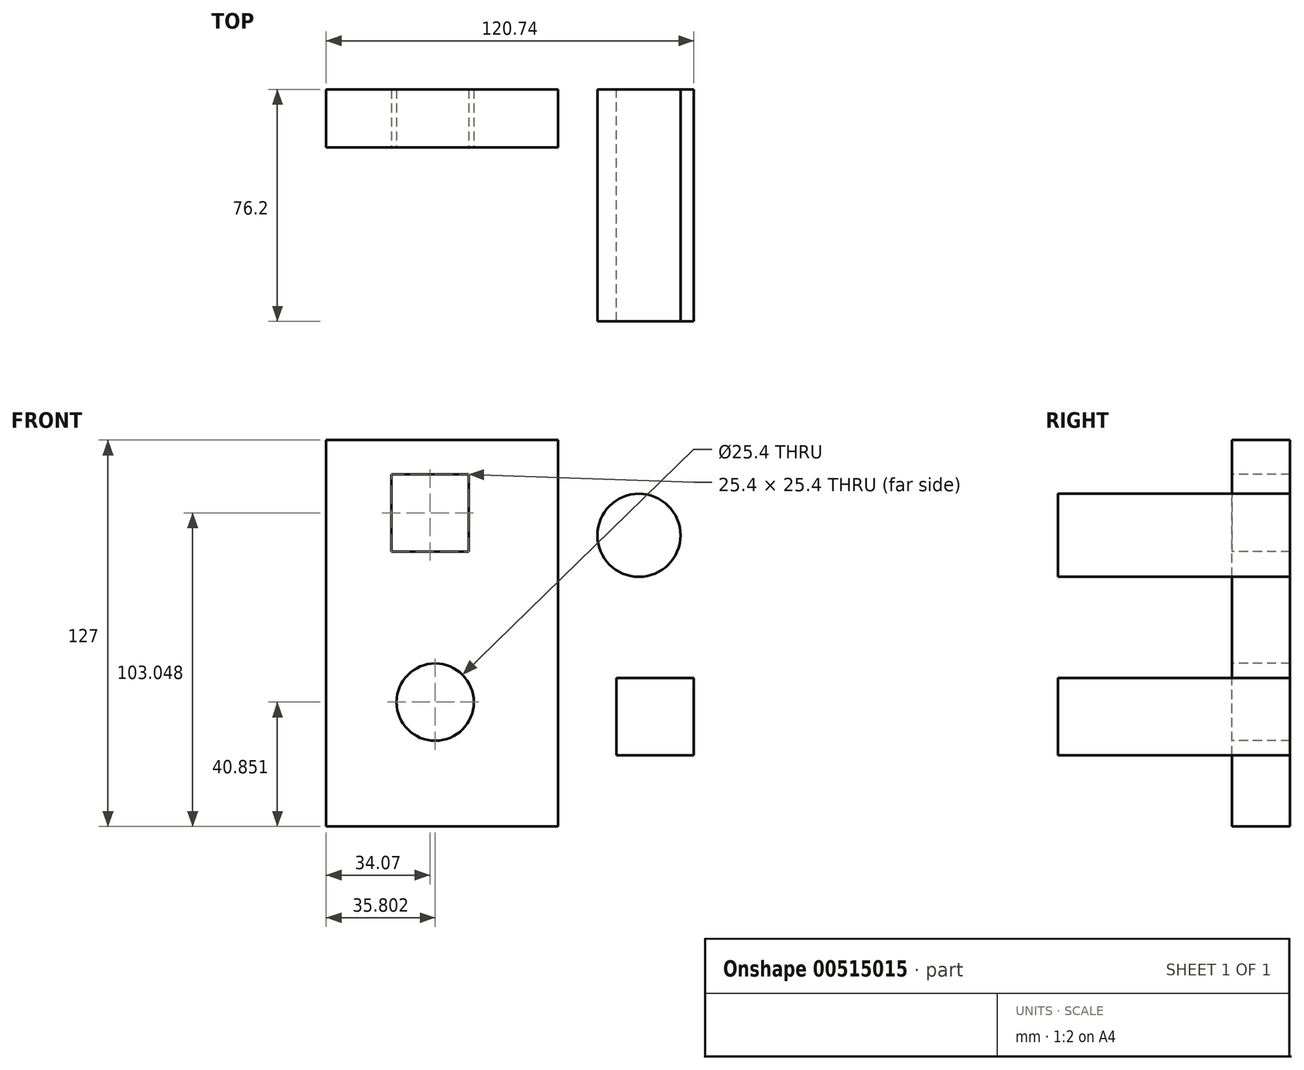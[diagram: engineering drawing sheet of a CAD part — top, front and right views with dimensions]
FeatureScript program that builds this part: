
annotation { "Feature Type Name" : "Feature", "Feature Type Description" : "" }
export const myFeature = defineFeature(function(context is Context, id is Id, definition is map)
    precondition{}
    {
        {
            var Q0;
            Q0=qCreatedBy(makeId("Front.planeOp"),FACE);
            var sketch = newSketch(context, id + "F0", { "sketchPlane" : qUnion([Q0])});
            skLineSegment(sketch, "E0", {"start": v(-71.8, 77.54) * mm, "end": v(-71.8, -49.46) * mm});
            skLineSegment(sketch, "E1", {"start": v(-71.8, -49.46) * mm, "end": v(4.4, -49.46) * mm});
            skLineSegment(sketch, "E2", {"start": v(4.4, -49.46) * mm, "end": v(4.4, 77.54) * mm});
            skLineSegment(sketch, "E3", {"start": v(4.4, 77.54) * mm, "end": v(-71.8, 77.54) * mm});
            skSolve(sketch);
        }
        {
            var Q0;
            Q0 = qSketchRegion(id + "F0", true);
            extrude(context, id + "F1", {"entities" : qUnion([Q0]), "depth" : 19.05 * mm, "offsetDistance" : 25.4 * mm});
        }
        {
            var Q0;
            Q0=makeQuery(id+"F1.opExtrude","CAP_FACE",FACE,{"disambiguationData":[OSD([sQuery(id+"F0.wireOp",EDGE,"E0"),sQuery(id+"F0.wireOp",EDGE,"E1"),sQuery(id+"F0.wireOp",EDGE,"E2"),sQuery(id+"F0.wireOp",EDGE,"E3")])],"isStart":false});
            var sketch = newSketch(context, id + "F2", { "sketchPlane" : qUnion([Q0])});
            skLineSegment(sketch, "E4.bottom", {"start": v(-50.43, 66.29) * mm, "end": v(-25.03, 66.29) * mm});
            skLineSegment(sketch, "E4.top", {"start": v(-50.43, 40.89) * mm, "end": v(-25.03, 40.89) * mm});
            skLineSegment(sketch, "E4.left", {"start": v(-50.43, 66.29) * mm, "end": v(-50.43, 40.89) * mm});
            skLineSegment(sketch, "E4.right", {"start": v(-25.03, 66.29) * mm, "end": v(-25.03, 40.89) * mm});
            skSolve(sketch);
        }
        {
            var Q0;
            Q0 = qSketchRegion(id + "F2", true);
            extrude(context, id + "F3", {"entities" : qUnion([Q0]), "operationType" : NewBodyOperationType.REMOVE, "oppositeDirection" : true, "depth" : 25.4 * mm, "offsetDistance" : 25.4 * mm});
        }
        {
            var Q0;
            Q0=makeQuery(id+"F1.opExtrude","CAP_FACE",FACE,{"disambiguationData":[OSD([sQuery(id+"F0.wireOp",EDGE,"E0"),sQuery(id+"F0.wireOp",EDGE,"E1"),sQuery(id+"F0.wireOp",EDGE,"E2"),sQuery(id+"F0.wireOp",EDGE,"E3")])],"isStart":false});
            var sketch = newSketch(context, id + "F4", { "sketchPlane" : qUnion([Q0])});
            skCircle(sketch, "E5", {"center": v(-36, -8.6) * mm, "radius": 12.7 * mm});
            skSolve(sketch);
        }
        {
            var Q0;
            Q0 = qSketchRegion(id + "F4", true);
            extrude(context, id + "F5", {"entities" : qUnion([Q0]), "operationType" : NewBodyOperationType.REMOVE, "oppositeDirection" : true, "depth" : 25.4 * mm, "offsetDistance" : 25.4 * mm});
        }
        {
            var Q0;
            Q0=qCreatedBy(makeId("Front.planeOp"),FACE);
            var sketch = newSketch(context, id + "F6", { "sketchPlane" : qUnion([Q0])});
            skCircle(sketch, "E6", {"center": v(30.94, 46.23) * mm, "radius": 13.64 * mm});
            skSolve(sketch);
        }
        {
            var Q0;
            Q0 = qSketchRegion(id + "F6", true);
            extrude(context, id + "F7", {"entities" : qUnion([Q0]), "depth" : 76.2 * mm, "offsetDistance" : 25.4 * mm});
        }
        {
            var Q0;
            Q0=qCreatedBy(makeId("Front.planeOp"),FACE);
            var sketch = newSketch(context, id + "F8", { "sketchPlane" : qUnion([Q0])});
            skLineSegment(sketch, "E7.bottom", {"start": v(23.54, -0.65) * mm, "end": v(48.94, -0.65) * mm});
            skLineSegment(sketch, "E7.top", {"start": v(23.54, -26.05) * mm, "end": v(48.94, -26.05) * mm});
            skLineSegment(sketch, "E7.left", {"start": v(23.54, -0.65) * mm, "end": v(23.54, -26.05) * mm});
            skLineSegment(sketch, "E7.right", {"start": v(48.94, -0.65) * mm, "end": v(48.94, -26.05) * mm});
            skSolve(sketch);
        }
        {
            var Q0;
            Q0 = qSketchRegion(id + "F8", true);
            extrude(context, id + "F9", {"entities" : qUnion([Q0]), "depth" : 76.2 * mm, "offsetDistance" : 25.4 * mm});
        }
    });
